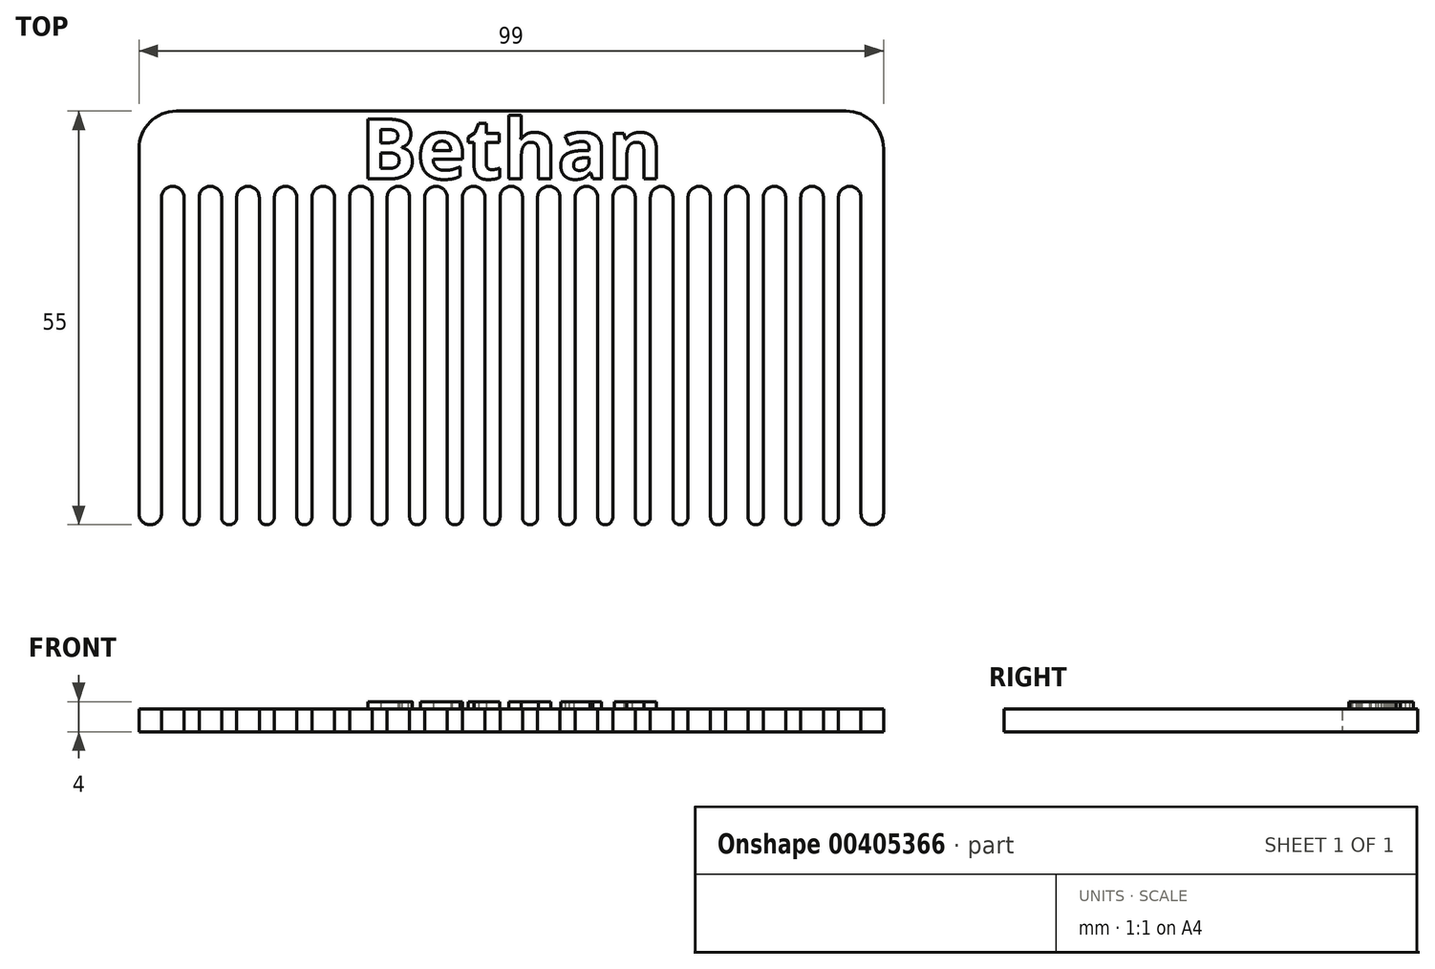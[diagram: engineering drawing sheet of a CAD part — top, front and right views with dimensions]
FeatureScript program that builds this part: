
annotation { "Feature Type Name" : "Feature", "Feature Type Description" : "" }
export const myFeature = defineFeature(function(context is Context, id is Id, definition is map)
    precondition{}
    {
        {
            var Q0;
            Q0=qCreatedBy(makeId("Top.planeOp"),FACE);
            var sketch = newSketch(context, id + "F0", { "sketchPlane" : qUnion([Q0])});
            skLineSegment(sketch, "E0.bottom", {"start": v(1.5, 0) * mm, "end": v(1.5, 0) * mm});
            skLineSegment(sketch, "E0.top", {"start": v(3, 55) * mm, "end": v(5, 55) * mm, "construction": true});
            skLineSegment(sketch, "E0.left", {"start": v(0, 1.5) * mm, "end": v(0, 50) * mm});
            skLineSegment(sketch, "E0.right", {"start": v(3, 1.5) * mm, "end": v(3, 43.5) * mm});
            skPoint(sketch, "E1.visualSharp", {"position": v(3, 0) * mm});
            skArc(sketch, "E1.filletArc", {"start": v(1.5, 0) * mm, "mid": v(2.56, 0.44) * mm, "end": v(3, 1.5) * mm});
            skPoint(sketch, "E2.visualSharp", {"position": v(0, 0) * mm});
            skArc(sketch, "E2.filletArc", {"start": v(0, 1.5) * mm, "mid": v(0.44, 0.44) * mm, "end": v(1.5, 0) * mm});
            skLineSegment(sketch, "E3.bottom", {"start": v(4.5, 45) * mm, "end": v(4.5, 45) * mm});
            skLineSegment(sketch, "E3.top", {"start": v(5, 55) * mm, "end": v(49.5, 55) * mm});
            skLineSegment(sketch, "E3.right", {"start": v(49.5, 45) * mm, "end": v(49.5, 55) * mm, "construction": true});
            skArc(sketch, "E4.MirrorCS", {"start": v(99, 1.5) * mm, "mid": v(98.56, 0.44) * mm, "end": v(97.5, 0) * mm});
            skArc(sketch, "E5.MirrorCS", {"start": v(97.5, 0) * mm, "mid": v(96.44, 0.44) * mm, "end": v(96, 1.5) * mm});
            skLineSegment(sketch, "E6.MirrorCS", {"start": v(96, 55) * mm, "end": v(94, 55) * mm, "construction": true});
            skPoint(sketch, "E7.MirrorP", {"position": v(96, 0) * mm});
            skPoint(sketch, "E8.MirrorP", {"position": v(99, 0) * mm});
            skLineSegment(sketch, "E9.MirrorCS", {"start": v(96, 1.5) * mm, "end": v(96, 43.5) * mm});
            skLineSegment(sketch, "E10.MirrorCS", {"start": v(94, 55) * mm, "end": v(49.5, 55) * mm});
            skLineSegment(sketch, "E11.MirrorCS", {"start": v(99, 1.5) * mm, "end": v(99, 50) * mm});
            skLineSegment(sketch, "E12.MirrorCS", {"start": v(94.5, 45) * mm, "end": v(94.5, 45) * mm});
            skLineSegment(sketch, "E13.top", {"start": v(7, 0) * mm, "end": v(7, 0) * mm});
            skLineSegment(sketch, "E13.left", {"start": v(6, 43.5) * mm, "end": v(6, 1) * mm});
            skLineSegment(sketch, "E13.right", {"start": v(8, 43.5) * mm, "end": v(8, 1) * mm});
            skPoint(sketch, "E14.visualSharp", {"position": v(8, 0) * mm});
            skArc(sketch, "E14.filletArc", {"start": v(7, 0) * mm, "mid": v(7.7, 0.3) * mm, "end": v(8, 1) * mm});
            skPoint(sketch, "E15.visualSharp", {"position": v(6, 0) * mm});
            skArc(sketch, "E15.filletArc", {"start": v(6, 1) * mm, "mid": v(6.3, 0.3) * mm, "end": v(7, 0) * mm});
            skLineSegment(sketch, "E16.trimOffspring", {"start": v(9.5, 45) * mm, "end": v(9.5, 45) * mm});
            skLineSegment(sketch, "E17.1.0.0", {"start": v(11, 43.5) * mm, "end": v(11, 1) * mm});
            skLineSegment(sketch, "E17.1.0.1", {"start": v(13, 43.5) * mm, "end": v(13, 1) * mm});
            skArc(sketch, "E17.1.0.2", {"start": v(12, 0) * mm, "mid": v(12.7, 0.3) * mm, "end": v(13, 1) * mm});
            skArc(sketch, "E17.1.0.3", {"start": v(11, 1) * mm, "mid": v(11.3, 0.3) * mm, "end": v(12, 0) * mm});
            skLineSegment(sketch, "E17.2.0.0", {"start": v(16, 43.5) * mm, "end": v(16, 1) * mm});
            skLineSegment(sketch, "E17.2.0.1", {"start": v(18, 43.5) * mm, "end": v(18, 1) * mm});
            skArc(sketch, "E17.2.0.2", {"start": v(17, 0) * mm, "mid": v(17.7, 0.3) * mm, "end": v(18, 1) * mm});
            skArc(sketch, "E17.2.0.3", {"start": v(16, 1) * mm, "mid": v(16.3, 0.3) * mm, "end": v(17, 0) * mm});
            skLineSegment(sketch, "E17.3.0.0", {"start": v(21, 43.5) * mm, "end": v(21, 1) * mm});
            skLineSegment(sketch, "E17.3.0.1", {"start": v(23, 43.5) * mm, "end": v(23, 1) * mm});
            skArc(sketch, "E17.3.0.2", {"start": v(22, 0) * mm, "mid": v(22.7, 0.3) * mm, "end": v(23, 1) * mm});
            skArc(sketch, "E17.3.0.3", {"start": v(21, 1) * mm, "mid": v(21.3, 0.3) * mm, "end": v(22, 0) * mm});
            skLineSegment(sketch, "E17.4.0.0", {"start": v(26, 43.5) * mm, "end": v(26, 1) * mm});
            skLineSegment(sketch, "E17.4.0.1", {"start": v(28, 43.5) * mm, "end": v(28, 1) * mm});
            skArc(sketch, "E17.4.0.2", {"start": v(27, 0) * mm, "mid": v(27.7, 0.3) * mm, "end": v(28, 1) * mm});
            skArc(sketch, "E17.4.0.3", {"start": v(26, 1) * mm, "mid": v(26.3, 0.3) * mm, "end": v(27, 0) * mm});
            skLineSegment(sketch, "E17.5.0.0", {"start": v(31, 43.5) * mm, "end": v(31, 1) * mm});
            skLineSegment(sketch, "E17.5.0.1", {"start": v(33, 43.5) * mm, "end": v(33, 1) * mm});
            skArc(sketch, "E17.5.0.2", {"start": v(32, 0) * mm, "mid": v(32.7, 0.3) * mm, "end": v(33, 1) * mm});
            skArc(sketch, "E17.5.0.3", {"start": v(31, 1) * mm, "mid": v(31.3, 0.3) * mm, "end": v(32, 0) * mm});
            skLineSegment(sketch, "E17.6.0.0", {"start": v(36, 43.5) * mm, "end": v(36, 1) * mm});
            skLineSegment(sketch, "E17.6.0.1", {"start": v(38, 43.5) * mm, "end": v(38, 1) * mm});
            skArc(sketch, "E17.6.0.2", {"start": v(37, 0) * mm, "mid": v(37.7, 0.3) * mm, "end": v(38, 1) * mm});
            skArc(sketch, "E17.6.0.3", {"start": v(36, 1) * mm, "mid": v(36.3, 0.3) * mm, "end": v(37, 0) * mm});
            skLineSegment(sketch, "E17.7.0.0", {"start": v(41, 43.5) * mm, "end": v(41, 1) * mm});
            skLineSegment(sketch, "E17.7.0.1", {"start": v(43, 43.5) * mm, "end": v(43, 1) * mm});
            skArc(sketch, "E17.7.0.2", {"start": v(42, 0) * mm, "mid": v(42.7, 0.3) * mm, "end": v(43, 1) * mm});
            skArc(sketch, "E17.7.0.3", {"start": v(41, 1) * mm, "mid": v(41.3, 0.3) * mm, "end": v(42, 0) * mm});
            skLineSegment(sketch, "E17.8.0.0", {"start": v(46, 43.5) * mm, "end": v(46, 1) * mm});
            skLineSegment(sketch, "E17.8.0.1", {"start": v(48, 43.5) * mm, "end": v(48, 1) * mm});
            skArc(sketch, "E17.8.0.2", {"start": v(47, 0) * mm, "mid": v(47.7, 0.3) * mm, "end": v(48, 1) * mm});
            skArc(sketch, "E17.8.0.3", {"start": v(46, 1) * mm, "mid": v(46.3, 0.3) * mm, "end": v(47, 0) * mm});
            skLineSegment(sketch, "E17.9.0.0", {"start": v(51, 43.5) * mm, "end": v(51, 1) * mm});
            skLineSegment(sketch, "E17.9.0.1", {"start": v(53, 43.5) * mm, "end": v(53, 1) * mm});
            skArc(sketch, "E17.9.0.2", {"start": v(52, 0) * mm, "mid": v(52.7, 0.3) * mm, "end": v(53, 1) * mm});
            skArc(sketch, "E17.9.0.3", {"start": v(51, 1) * mm, "mid": v(51.3, 0.3) * mm, "end": v(52, 0) * mm});
            skLineSegment(sketch, "E17.10.0.0", {"start": v(56, 43.5) * mm, "end": v(56, 1) * mm});
            skLineSegment(sketch, "E17.10.0.1", {"start": v(58, 43.5) * mm, "end": v(58, 1) * mm});
            skArc(sketch, "E17.10.0.2", {"start": v(57, 0) * mm, "mid": v(57.7, 0.3) * mm, "end": v(58, 1) * mm});
            skArc(sketch, "E17.10.0.3", {"start": v(56, 1) * mm, "mid": v(56.3, 0.3) * mm, "end": v(57, 0) * mm});
            skLineSegment(sketch, "E17.11.0.0", {"start": v(61, 43.5) * mm, "end": v(61, 1) * mm});
            skLineSegment(sketch, "E17.11.0.1", {"start": v(63, 43.5) * mm, "end": v(63, 1) * mm});
            skArc(sketch, "E17.11.0.2", {"start": v(62, 0) * mm, "mid": v(62.7, 0.3) * mm, "end": v(63, 1) * mm});
            skArc(sketch, "E17.11.0.3", {"start": v(61, 1) * mm, "mid": v(61.3, 0.3) * mm, "end": v(62, 0) * mm});
            skLineSegment(sketch, "E17.12.0.0", {"start": v(66, 43.5) * mm, "end": v(66, 1) * mm});
            skLineSegment(sketch, "E17.12.0.1", {"start": v(68, 43.5) * mm, "end": v(68, 1) * mm});
            skArc(sketch, "E17.12.0.2", {"start": v(67, 0) * mm, "mid": v(67.7, 0.3) * mm, "end": v(68, 1) * mm});
            skArc(sketch, "E17.12.0.3", {"start": v(66, 1) * mm, "mid": v(66.3, 0.3) * mm, "end": v(67, 0) * mm});
            skLineSegment(sketch, "E17.13.0.0", {"start": v(71, 43.5) * mm, "end": v(71, 1) * mm});
            skLineSegment(sketch, "E17.13.0.1", {"start": v(73, 43.5) * mm, "end": v(73, 1) * mm});
            skArc(sketch, "E17.13.0.2", {"start": v(72, 0) * mm, "mid": v(72.7, 0.3) * mm, "end": v(73, 1) * mm});
            skArc(sketch, "E17.13.0.3", {"start": v(71, 1) * mm, "mid": v(71.3, 0.3) * mm, "end": v(72, 0) * mm});
            skLineSegment(sketch, "E17.14.0.0", {"start": v(76, 43.5) * mm, "end": v(76, 1) * mm});
            skLineSegment(sketch, "E17.14.0.1", {"start": v(78, 43.5) * mm, "end": v(78, 1) * mm});
            skArc(sketch, "E17.14.0.2", {"start": v(77, 0) * mm, "mid": v(77.7, 0.3) * mm, "end": v(78, 1) * mm});
            skArc(sketch, "E17.14.0.3", {"start": v(76, 1) * mm, "mid": v(76.3, 0.3) * mm, "end": v(77, 0) * mm});
            skLineSegment(sketch, "E17.15.0.0", {"start": v(81, 43.5) * mm, "end": v(81, 1) * mm});
            skLineSegment(sketch, "E17.15.0.1", {"start": v(83, 43.5) * mm, "end": v(83, 1) * mm});
            skArc(sketch, "E17.15.0.2", {"start": v(82, 0) * mm, "mid": v(82.7, 0.3) * mm, "end": v(83, 1) * mm});
            skArc(sketch, "E17.15.0.3", {"start": v(81, 1) * mm, "mid": v(81.3, 0.3) * mm, "end": v(82, 0) * mm});
            skLineSegment(sketch, "E17.16.0.0", {"start": v(86, 43.5) * mm, "end": v(86, 1) * mm});
            skLineSegment(sketch, "E17.16.0.1", {"start": v(88, 43.5) * mm, "end": v(88, 1) * mm});
            skArc(sketch, "E17.16.0.2", {"start": v(87, 0) * mm, "mid": v(87.7, 0.3) * mm, "end": v(88, 1) * mm});
            skArc(sketch, "E17.16.0.3", {"start": v(86, 1) * mm, "mid": v(86.3, 0.3) * mm, "end": v(87, 0) * mm});
            skLineSegment(sketch, "E17.17.0.0", {"start": v(91, 43.5) * mm, "end": v(91, 1) * mm});
            skLineSegment(sketch, "E17.17.0.1", {"start": v(93, 43.5) * mm, "end": v(93, 1) * mm});
            skArc(sketch, "E17.17.0.2", {"start": v(92, 0) * mm, "mid": v(92.7, 0.3) * mm, "end": v(93, 1) * mm});
            skArc(sketch, "E17.17.0.3", {"start": v(91, 1) * mm, "mid": v(91.3, 0.3) * mm, "end": v(92, 0) * mm});
            skLineSegment(sketch, "E17.direction1", {"start": v(7, 0) * mm, "end": v(12, 0) * mm, "construction": true});
            skPoint(sketch, "E18.visualSharp", {"position": v(99, 55) * mm});
            skArc(sketch, "E18.filletArc", {"start": v(99, 50) * mm, "mid": v(97.54, 53.54) * mm, "end": v(94, 55) * mm});
            skPoint(sketch, "E19.visualSharp", {"position": v(0, 55) * mm});
            skArc(sketch, "E19.filletArc", {"start": v(5, 55) * mm, "mid": v(1.46, 53.54) * mm, "end": v(0, 50) * mm});
            skLineSegment(sketch, "E20.trimOffspring", {"start": v(14.5, 45) * mm, "end": v(14.5, 45) * mm});
            skLineSegment(sketch, "E21.trimOffspring", {"start": v(19.5, 45) * mm, "end": v(19.5, 45) * mm});
            skLineSegment(sketch, "E22.trimOffspring", {"start": v(24.5, 45) * mm, "end": v(24.5, 45) * mm});
            skLineSegment(sketch, "E23.trimOffspring", {"start": v(29.5, 45) * mm, "end": v(29.5, 45) * mm});
            skLineSegment(sketch, "E24.trimOffspring", {"start": v(34.5, 45) * mm, "end": v(34.5, 45) * mm});
            skLineSegment(sketch, "E25.trimOffspring", {"start": v(39.5, 45) * mm, "end": v(39.5, 45) * mm});
            skLineSegment(sketch, "E26.trimOffspring", {"start": v(44.5, 45) * mm, "end": v(44.5, 45) * mm});
            skLineSegment(sketch, "E27.trimOffspring", {"start": v(49.5, 45) * mm, "end": v(49.5, 45) * mm});
            skLineSegment(sketch, "E28.trimOffspring", {"start": v(54.5, 45) * mm, "end": v(54.5, 45) * mm});
            skLineSegment(sketch, "E29.trimOffspring", {"start": v(59.5, 45) * mm, "end": v(59.5, 45) * mm});
            skLineSegment(sketch, "E30.trimOffspring", {"start": v(64.5, 45) * mm, "end": v(64.5, 45) * mm});
            skLineSegment(sketch, "E31.trimOffspring", {"start": v(69.5, 45) * mm, "end": v(69.5, 45) * mm});
            skLineSegment(sketch, "E32.trimOffspring", {"start": v(74.5, 45) * mm, "end": v(74.5, 45) * mm});
            skLineSegment(sketch, "E33.trimOffspring", {"start": v(79.5, 45) * mm, "end": v(79.5, 45) * mm});
            skLineSegment(sketch, "E34.trimOffspring", {"start": v(84.5, 45) * mm, "end": v(84.5, 45) * mm});
            skLineSegment(sketch, "E35.trimOffspring", {"start": v(89.5, 45) * mm, "end": v(89.5, 45) * mm});
            skPoint(sketch, "E36.orphan", {"position": v(96, 55) * mm});
            skPoint(sketch, "E37.visualSharp", {"position": v(3, 45) * mm});
            skArc(sketch, "E37.filletArc", {"start": v(4.5, 45) * mm, "mid": v(3.44, 44.56) * mm, "end": v(3, 43.5) * mm});
            skPoint(sketch, "E38.visualSharp", {"position": v(6, 45) * mm});
            skArc(sketch, "E38.filletArc", {"start": v(6, 43.5) * mm, "mid": v(5.56, 44.56) * mm, "end": v(4.5, 45) * mm});
            skPoint(sketch, "E39.visualSharp", {"position": v(8, 45) * mm});
            skArc(sketch, "E39.filletArc", {"start": v(9.5, 45) * mm, "mid": v(8.44, 44.56) * mm, "end": v(8, 43.5) * mm});
            skPoint(sketch, "E40.visualSharp", {"position": v(11, 45) * mm});
            skArc(sketch, "E40.filletArc", {"start": v(11, 43.5) * mm, "mid": v(10.56, 44.56) * mm, "end": v(9.5, 45) * mm});
            skPoint(sketch, "E41.visualSharp", {"position": v(13, 45) * mm});
            skArc(sketch, "E41.filletArc", {"start": v(14.5, 45) * mm, "mid": v(13.44, 44.56) * mm, "end": v(13, 43.5) * mm});
            skPoint(sketch, "E42.visualSharp", {"position": v(16, 45) * mm});
            skArc(sketch, "E42.filletArc", {"start": v(16, 43.5) * mm, "mid": v(15.56, 44.56) * mm, "end": v(14.5, 45) * mm});
            skPoint(sketch, "E43.visualSharp", {"position": v(18, 45) * mm});
            skArc(sketch, "E43.filletArc", {"start": v(19.5, 45) * mm, "mid": v(18.44, 44.56) * mm, "end": v(18, 43.5) * mm});
            skPoint(sketch, "E44.visualSharp", {"position": v(21, 45) * mm});
            skArc(sketch, "E44.filletArc", {"start": v(21, 43.5) * mm, "mid": v(20.56, 44.56) * mm, "end": v(19.5, 45) * mm});
            skPoint(sketch, "E45.visualSharp", {"position": v(23, 45) * mm});
            skArc(sketch, "E45.filletArc", {"start": v(24.5, 45) * mm, "mid": v(23.44, 44.56) * mm, "end": v(23, 43.5) * mm});
            skPoint(sketch, "E46.visualSharp", {"position": v(26, 45) * mm});
            skArc(sketch, "E46.filletArc", {"start": v(26, 43.5) * mm, "mid": v(25.56, 44.56) * mm, "end": v(24.5, 45) * mm});
            skPoint(sketch, "E47.visualSharp", {"position": v(28, 45) * mm});
            skArc(sketch, "E47.filletArc", {"start": v(29.5, 45) * mm, "mid": v(28.44, 44.56) * mm, "end": v(28, 43.5) * mm});
            skPoint(sketch, "E48.visualSharp", {"position": v(31, 45) * mm});
            skArc(sketch, "E48.filletArc", {"start": v(31, 43.5) * mm, "mid": v(30.56, 44.56) * mm, "end": v(29.5, 45) * mm});
            skPoint(sketch, "E49.visualSharp", {"position": v(33, 45) * mm});
            skArc(sketch, "E49.filletArc", {"start": v(34.5, 45) * mm, "mid": v(33.44, 44.56) * mm, "end": v(33, 43.5) * mm});
            skPoint(sketch, "E50.visualSharp", {"position": v(36, 45) * mm});
            skArc(sketch, "E50.filletArc", {"start": v(36, 43.5) * mm, "mid": v(35.56, 44.56) * mm, "end": v(34.5, 45) * mm});
            skPoint(sketch, "E51.visualSharp", {"position": v(38, 45) * mm});
            skArc(sketch, "E51.filletArc", {"start": v(39.5, 45) * mm, "mid": v(38.44, 44.56) * mm, "end": v(38, 43.5) * mm});
            skPoint(sketch, "E52.visualSharp", {"position": v(41, 45) * mm});
            skArc(sketch, "E52.filletArc", {"start": v(41, 43.5) * mm, "mid": v(40.56, 44.56) * mm, "end": v(39.5, 45) * mm});
            skPoint(sketch, "E53.visualSharp", {"position": v(43, 45) * mm});
            skArc(sketch, "E53.filletArc", {"start": v(44.5, 45) * mm, "mid": v(43.44, 44.56) * mm, "end": v(43, 43.5) * mm});
            skPoint(sketch, "E54.visualSharp", {"position": v(46, 45) * mm});
            skArc(sketch, "E54.filletArc", {"start": v(46, 43.5) * mm, "mid": v(45.56, 44.56) * mm, "end": v(44.5, 45) * mm});
            skPoint(sketch, "E55.visualSharp", {"position": v(48, 45) * mm});
            skArc(sketch, "E55.filletArc", {"start": v(49.5, 45) * mm, "mid": v(48.44, 44.56) * mm, "end": v(48, 43.5) * mm});
            skPoint(sketch, "E56.visualSharp", {"position": v(51, 45) * mm});
            skArc(sketch, "E56.filletArc", {"start": v(51, 43.5) * mm, "mid": v(50.56, 44.56) * mm, "end": v(49.5, 45) * mm});
            skPoint(sketch, "E57.visualSharp", {"position": v(53, 45) * mm});
            skArc(sketch, "E57.filletArc", {"start": v(54.5, 45) * mm, "mid": v(53.44, 44.56) * mm, "end": v(53, 43.5) * mm});
            skPoint(sketch, "E58.visualSharp", {"position": v(56, 45) * mm});
            skArc(sketch, "E58.filletArc", {"start": v(56, 43.5) * mm, "mid": v(55.56, 44.56) * mm, "end": v(54.5, 45) * mm});
            skPoint(sketch, "E59.visualSharp", {"position": v(96, 45) * mm});
            skArc(sketch, "E59.filletArc", {"start": v(96, 43.5) * mm, "mid": v(95.56, 44.56) * mm, "end": v(94.5, 45) * mm});
            skPoint(sketch, "E60.visualSharp", {"position": v(93, 45) * mm});
            skArc(sketch, "E60.filletArc", {"start": v(94.5, 45) * mm, "mid": v(93.44, 44.56) * mm, "end": v(93, 43.5) * mm});
            skPoint(sketch, "E61.visualSharp", {"position": v(91, 45) * mm});
            skArc(sketch, "E61.filletArc", {"start": v(91, 43.5) * mm, "mid": v(90.56, 44.56) * mm, "end": v(89.5, 45) * mm});
            skPoint(sketch, "E62.visualSharp", {"position": v(88, 45) * mm});
            skArc(sketch, "E62.filletArc", {"start": v(89.5, 45) * mm, "mid": v(88.44, 44.56) * mm, "end": v(88, 43.5) * mm});
            skPoint(sketch, "E63.visualSharp", {"position": v(86, 45) * mm});
            skArc(sketch, "E63.filletArc", {"start": v(86, 43.5) * mm, "mid": v(85.56, 44.56) * mm, "end": v(84.5, 45) * mm});
            skPoint(sketch, "E64.visualSharp", {"position": v(83, 45) * mm});
            skArc(sketch, "E64.filletArc", {"start": v(84.5, 45) * mm, "mid": v(83.44, 44.56) * mm, "end": v(83, 43.5) * mm});
            skPoint(sketch, "E65.visualSharp", {"position": v(81, 45) * mm});
            skArc(sketch, "E65.filletArc", {"start": v(81, 43.5) * mm, "mid": v(80.56, 44.56) * mm, "end": v(79.5, 45) * mm});
            skPoint(sketch, "E66.visualSharp", {"position": v(78, 45) * mm});
            skArc(sketch, "E66.filletArc", {"start": v(79.5, 45) * mm, "mid": v(78.44, 44.56) * mm, "end": v(78, 43.5) * mm});
            skPoint(sketch, "E67.visualSharp", {"position": v(76, 45) * mm});
            skArc(sketch, "E67.filletArc", {"start": v(76, 43.5) * mm, "mid": v(75.56, 44.56) * mm, "end": v(74.5, 45) * mm});
            skPoint(sketch, "E68.visualSharp", {"position": v(73, 45) * mm});
            skArc(sketch, "E68.filletArc", {"start": v(74.5, 45) * mm, "mid": v(73.44, 44.56) * mm, "end": v(73, 43.5) * mm});
            skPoint(sketch, "E69.visualSharp", {"position": v(68, 45) * mm});
            skArc(sketch, "E69.filletArc", {"start": v(69.5, 45) * mm, "mid": v(68.44, 44.56) * mm, "end": v(68, 43.5) * mm});
            skPoint(sketch, "E70.visualSharp", {"position": v(71, 45) * mm});
            skArc(sketch, "E70.filletArc", {"start": v(71, 43.5) * mm, "mid": v(70.56, 44.56) * mm, "end": v(69.5, 45) * mm});
            skPoint(sketch, "E71.visualSharp", {"position": v(66, 45) * mm});
            skArc(sketch, "E71.filletArc", {"start": v(66, 43.5) * mm, "mid": v(65.56, 44.56) * mm, "end": v(64.5, 45) * mm});
            skPoint(sketch, "E72.visualSharp", {"position": v(63, 45) * mm});
            skArc(sketch, "E72.filletArc", {"start": v(64.5, 45) * mm, "mid": v(63.44, 44.56) * mm, "end": v(63, 43.5) * mm});
            skPoint(sketch, "E73.visualSharp", {"position": v(61, 45) * mm});
            skArc(sketch, "E73.filletArc", {"start": v(61, 43.5) * mm, "mid": v(60.56, 44.56) * mm, "end": v(59.5, 45) * mm});
            skPoint(sketch, "E74.visualSharp", {"position": v(58, 45) * mm});
            skArc(sketch, "E74.filletArc", {"start": v(59.5, 45) * mm, "mid": v(58.44, 44.56) * mm, "end": v(58, 43.5) * mm});
            skSolve(sketch);
        }
        {
            var Q0;
            Q0 = qSketchRegion(id + "F0", true);
            extrude(context, id + "F1", {"entities" : qUnion([Q0]), "depth" : 3 * mm});
        }
        {
            var Q0;
            Q0=makeQuery(id+"F1.opExtrude","CAP_FACE",FACE,{"disambiguationData":[OSD([sQuery(id+"F0.wireOp",EDGE,"E0.left"),sQuery(id+"F0.wireOp",EDGE,"E0.right"),sQuery(id+"F0.wireOp",EDGE,"E1.filletArc"),sQuery(id+"F0.wireOp",EDGE,"E2.filletArc"),sQuery(id+"F0.wireOp",EDGE,"E3.top"),sQuery(id+"F0.wireOp",EDGE,"E4.MirrorCS"),sQuery(id+"F0.wireOp",EDGE,"E5.MirrorCS"),sQuery(id+"F0.wireOp",EDGE,"E9.MirrorCS"),sQuery(id+"F0.wireOp",EDGE,"E10.MirrorCS"),sQuery(id+"F0.wireOp",EDGE,"E11.MirrorCS"),sQuery(id+"F0.wireOp",EDGE,"E13.left"),sQuery(id+"F0.wireOp",EDGE,"E13.right"),sQuery(id+"F0.wireOp",EDGE,"E14.filletArc"),sQuery(id+"F0.wireOp",EDGE,"E15.filletArc"),sQuery(id+"F0.wireOp",EDGE,"E17.1.0.0"),sQuery(id+"F0.wireOp",EDGE,"E17.1.0.1"),sQuery(id+"F0.wireOp",EDGE,"E17.1.0.2"),sQuery(id+"F0.wireOp",EDGE,"E17.1.0.3"),sQuery(id+"F0.wireOp",EDGE,"E17.2.0.0"),sQuery(id+"F0.wireOp",EDGE,"E17.2.0.1"),sQuery(id+"F0.wireOp",EDGE,"E17.2.0.2"),sQuery(id+"F0.wireOp",EDGE,"E17.2.0.3"),sQuery(id+"F0.wireOp",EDGE,"E17.3.0.0"),sQuery(id+"F0.wireOp",EDGE,"E17.3.0.1"),sQuery(id+"F0.wireOp",EDGE,"E17.3.0.2"),sQuery(id+"F0.wireOp",EDGE,"E17.3.0.3"),sQuery(id+"F0.wireOp",EDGE,"E17.4.0.0"),sQuery(id+"F0.wireOp",EDGE,"E17.4.0.1"),sQuery(id+"F0.wireOp",EDGE,"E17.4.0.2"),sQuery(id+"F0.wireOp",EDGE,"E17.4.0.3"),sQuery(id+"F0.wireOp",EDGE,"E17.5.0.0"),sQuery(id+"F0.wireOp",EDGE,"E17.5.0.1"),sQuery(id+"F0.wireOp",EDGE,"E17.5.0.2"),sQuery(id+"F0.wireOp",EDGE,"E17.5.0.3"),sQuery(id+"F0.wireOp",EDGE,"E17.6.0.0"),sQuery(id+"F0.wireOp",EDGE,"E17.6.0.1"),sQuery(id+"F0.wireOp",EDGE,"E17.6.0.2"),sQuery(id+"F0.wireOp",EDGE,"E17.6.0.3"),sQuery(id+"F0.wireOp",EDGE,"E17.7.0.0"),sQuery(id+"F0.wireOp",EDGE,"E17.7.0.1"),sQuery(id+"F0.wireOp",EDGE,"E17.7.0.2"),sQuery(id+"F0.wireOp",EDGE,"E17.7.0.3"),sQuery(id+"F0.wireOp",EDGE,"E17.8.0.0"),sQuery(id+"F0.wireOp",EDGE,"E17.8.0.1"),sQuery(id+"F0.wireOp",EDGE,"E17.8.0.2"),sQuery(id+"F0.wireOp",EDGE,"E17.8.0.3"),sQuery(id+"F0.wireOp",EDGE,"E17.9.0.0"),sQuery(id+"F0.wireOp",EDGE,"E17.9.0.1"),sQuery(id+"F0.wireOp",EDGE,"E17.9.0.2"),sQuery(id+"F0.wireOp",EDGE,"E17.9.0.3"),sQuery(id+"F0.wireOp",EDGE,"E17.10.0.0"),sQuery(id+"F0.wireOp",EDGE,"E17.10.0.1"),sQuery(id+"F0.wireOp",EDGE,"E17.10.0.2"),sQuery(id+"F0.wireOp",EDGE,"E17.10.0.3"),sQuery(id+"F0.wireOp",EDGE,"E17.11.0.0"),sQuery(id+"F0.wireOp",EDGE,"E17.11.0.1"),sQuery(id+"F0.wireOp",EDGE,"E17.11.0.2"),sQuery(id+"F0.wireOp",EDGE,"E17.11.0.3"),sQuery(id+"F0.wireOp",EDGE,"E17.12.0.0"),sQuery(id+"F0.wireOp",EDGE,"E17.12.0.1"),sQuery(id+"F0.wireOp",EDGE,"E17.12.0.2"),sQuery(id+"F0.wireOp",EDGE,"E17.12.0.3"),sQuery(id+"F0.wireOp",EDGE,"E17.13.0.0"),sQuery(id+"F0.wireOp",EDGE,"E17.13.0.1"),sQuery(id+"F0.wireOp",EDGE,"E17.13.0.2"),sQuery(id+"F0.wireOp",EDGE,"E17.13.0.3"),sQuery(id+"F0.wireOp",EDGE,"E17.14.0.0"),sQuery(id+"F0.wireOp",EDGE,"E17.14.0.1"),sQuery(id+"F0.wireOp",EDGE,"E17.14.0.2"),sQuery(id+"F0.wireOp",EDGE,"E17.14.0.3"),sQuery(id+"F0.wireOp",EDGE,"E17.15.0.0"),sQuery(id+"F0.wireOp",EDGE,"E17.15.0.1"),sQuery(id+"F0.wireOp",EDGE,"E17.15.0.2"),sQuery(id+"F0.wireOp",EDGE,"E17.15.0.3"),sQuery(id+"F0.wireOp",EDGE,"E17.16.0.0"),sQuery(id+"F0.wireOp",EDGE,"E17.16.0.1"),sQuery(id+"F0.wireOp",EDGE,"E17.16.0.2"),sQuery(id+"F0.wireOp",EDGE,"E17.16.0.3"),sQuery(id+"F0.wireOp",EDGE,"E17.17.0.0"),sQuery(id+"F0.wireOp",EDGE,"E17.17.0.1"),sQuery(id+"F0.wireOp",EDGE,"E17.17.0.2"),sQuery(id+"F0.wireOp",EDGE,"E17.17.0.3"),sQuery(id+"F0.wireOp",EDGE,"E18.filletArc"),sQuery(id+"F0.wireOp",EDGE,"E19.filletArc"),sQuery(id+"F0.wireOp",EDGE,"E37.filletArc"),sQuery(id+"F0.wireOp",EDGE,"E38.filletArc"),sQuery(id+"F0.wireOp",EDGE,"E39.filletArc"),sQuery(id+"F0.wireOp",EDGE,"E40.filletArc"),sQuery(id+"F0.wireOp",EDGE,"E41.filletArc"),sQuery(id+"F0.wireOp",EDGE,"E42.filletArc"),sQuery(id+"F0.wireOp",EDGE,"E43.filletArc"),sQuery(id+"F0.wireOp",EDGE,"E44.filletArc"),sQuery(id+"F0.wireOp",EDGE,"E45.filletArc"),sQuery(id+"F0.wireOp",EDGE,"E46.filletArc"),sQuery(id+"F0.wireOp",EDGE,"E47.filletArc"),sQuery(id+"F0.wireOp",EDGE,"E48.filletArc"),sQuery(id+"F0.wireOp",EDGE,"E49.filletArc"),sQuery(id+"F0.wireOp",EDGE,"E50.filletArc"),sQuery(id+"F0.wireOp",EDGE,"E51.filletArc"),sQuery(id+"F0.wireOp",EDGE,"E52.filletArc"),sQuery(id+"F0.wireOp",EDGE,"E53.filletArc"),sQuery(id+"F0.wireOp",EDGE,"E54.filletArc"),sQuery(id+"F0.wireOp",EDGE,"E55.filletArc"),sQuery(id+"F0.wireOp",EDGE,"E56.filletArc"),sQuery(id+"F0.wireOp",EDGE,"E57.filletArc"),sQuery(id+"F0.wireOp",EDGE,"E58.filletArc"),sQuery(id+"F0.wireOp",EDGE,"E59.filletArc"),sQuery(id+"F0.wireOp",EDGE,"E60.filletArc"),sQuery(id+"F0.wireOp",EDGE,"E61.filletArc"),sQuery(id+"F0.wireOp",EDGE,"E62.filletArc"),sQuery(id+"F0.wireOp",EDGE,"E63.filletArc"),sQuery(id+"F0.wireOp",EDGE,"E64.filletArc"),sQuery(id+"F0.wireOp",EDGE,"E65.filletArc"),sQuery(id+"F0.wireOp",EDGE,"E66.filletArc"),sQuery(id+"F0.wireOp",EDGE,"E67.filletArc"),sQuery(id+"F0.wireOp",EDGE,"E68.filletArc"),sQuery(id+"F0.wireOp",EDGE,"E69.filletArc"),sQuery(id+"F0.wireOp",EDGE,"E70.filletArc"),sQuery(id+"F0.wireOp",EDGE,"E71.filletArc"),sQuery(id+"F0.wireOp",EDGE,"E72.filletArc"),sQuery(id+"F0.wireOp",EDGE,"E73.filletArc"),sQuery(id+"F0.wireOp",EDGE,"E74.filletArc")])],"isStart":false});
            var sketch = newSketch(context, id + "F2", { "sketchPlane" : qUnion([Q0])});
            skText(sketch, "E75", { "text": "Bethan", "fontName": "OpenSans-Bold.ttf"});
            skLineSegment(sketch, "E76", {"start": v(14.5, 45) * mm, "end": v(14.5, 55) * mm, "construction": true});
            skPoint(sketch, "E77", {"position": v(14.5, 50) * mm});
            skPoint(sketch, "E78", {"position": v(29.47, 50) * mm});
            const initialGuessF2  = {"E75": [0.02947, 0.046, 1, 0, 0.008]};
            skSetInitialGuess(sketch, initialGuessF2);
            skSolve(sketch);
        }
        {
            var Q0;
            Q0 = qSketchRegion(id + "F2", true);
            extrude(context, id + "F3", {"entities" : qUnion([Q0]), "operationType" : NewBodyOperationType.ADD, "depth" : 1 * mm});
        }
    });
